# Revit family: Digidim  Imagine 8 Channel X 10 Amp Relay Unit_498
name_source: partatom
category: Electrical Fixtures
revit_build: Autodesk Revit 2018 (Build: 20170223_1515(x64)
units: mm (PartAtom-declared; Revit-internal decimal feet)

## family parameters
Always vertical = Yes
Cut with Voids When Loaded = No
Maintain Annotation Orientation = No
OmniClass Number = 23.80.00.00
OmniClass Title = Electric Power and Lighting
Part Type = Normal
Room Calculation Point = No
Round Connector Dimension = Use Diameter
Shared = No
Work Plane-Based = Yes

## types (1)
- Digidim  Imagine 8 Channel X 16 Amp Relay Unit
    Ambient temperature = 0 °C to + 40 °C
    Channels = 8 (2 channels per four-way connector)
    Communication = DALI, SDIM and DMX
    Connections: = Mains/relay: Up to 4 mm² solid or up to 2.5 mm² stranded
DALI: 0.5 mm² – 1.5 mm² solid or stranded.
            Max. length: 300 m @ 1.5 mm².
SDIM/DMX: 0.22 mm² – 1.5 mm² low-loss RS485
                  type (multistranded, twisted and shielded). Max. length: 1000 m (lowloss cable). Examples: Belden 8102
                  or Alpha 6222C.
                  Note: One twisted pair for A and B
                 (85 Ω to 100 Ω impedance), one core
                  or twisted pair for 0 V, and shield for screen.
Cable rating: Mains cables, relay cables and DALI
                   cables must be mains rated.
    DALI consumption = 2 mA
    DALI: = DALI standard IEC 60929, with Helvar additions
    DMX = DMX512-A protocol (max. refresh
rate: 33 Hz
    Default Elevation = 0 mm  [stored 0 ft]
    Dimensions: = 160 mm × 90 mm × 58 mm
    EMC emission = EN 55015
    EMC immunity = EN 61547
    Environment = Complies with WEEE and RoHS directives.
    External protection = The mains supply must be
protected at 6 A maximum. The
relays must be protected by a
16 A Type C MCB maximum.
    Housing = Plastic (polycarbonate) DIN-rail case
    IP code: = IP30 (IP00 at terminals)
    Internal losses = 2.1 W + max. 1.6 W per channel
    Isolation = Between every connector, with this
exception: ‘SDIM 0 V’ and ‘OVR 0 V’
are not isolated from each other.
    Mains Supply = 100 VAC – 240 VAC (nominal)
85 VAC – 264 VAC (absolute)
45 Hz – 65 Hz
    Manufacturer = Helvar
    Model = 498
    Mounting = DIN rail (installation in
switchgear/controlgear cabinet)
    Number of devices = For ballasts, quantity is limited by
MCB; refer to manufacturer’s data.
These are power relays and therefore
not suitable for extra-low voltage
operation.
Where power relays are used to
control contactors, make sure that
snubbers are fitted
    Override = Wired override input
    Power consumption = 2.6 W
    Relative humidity = Max. 90 %, noncondensing
    Relay voltage = 240 VAC (400 VAC between channels)
    SDIM: = Helvar SDIM protocol
    Safety = EN 61347-2-11
    Standby power consumption: = 1.1 W
    Storage temperature = −10 °C to + 70 °C
    Weight: = 400 g

note: [stored X ft] marks values corroborated as IEEE doubles in the binary element streams (Revit-internal decimal feet)

## geometry (parser evidence)
native form markers: Sweep x2
no freeform markers — native parametric forms only
